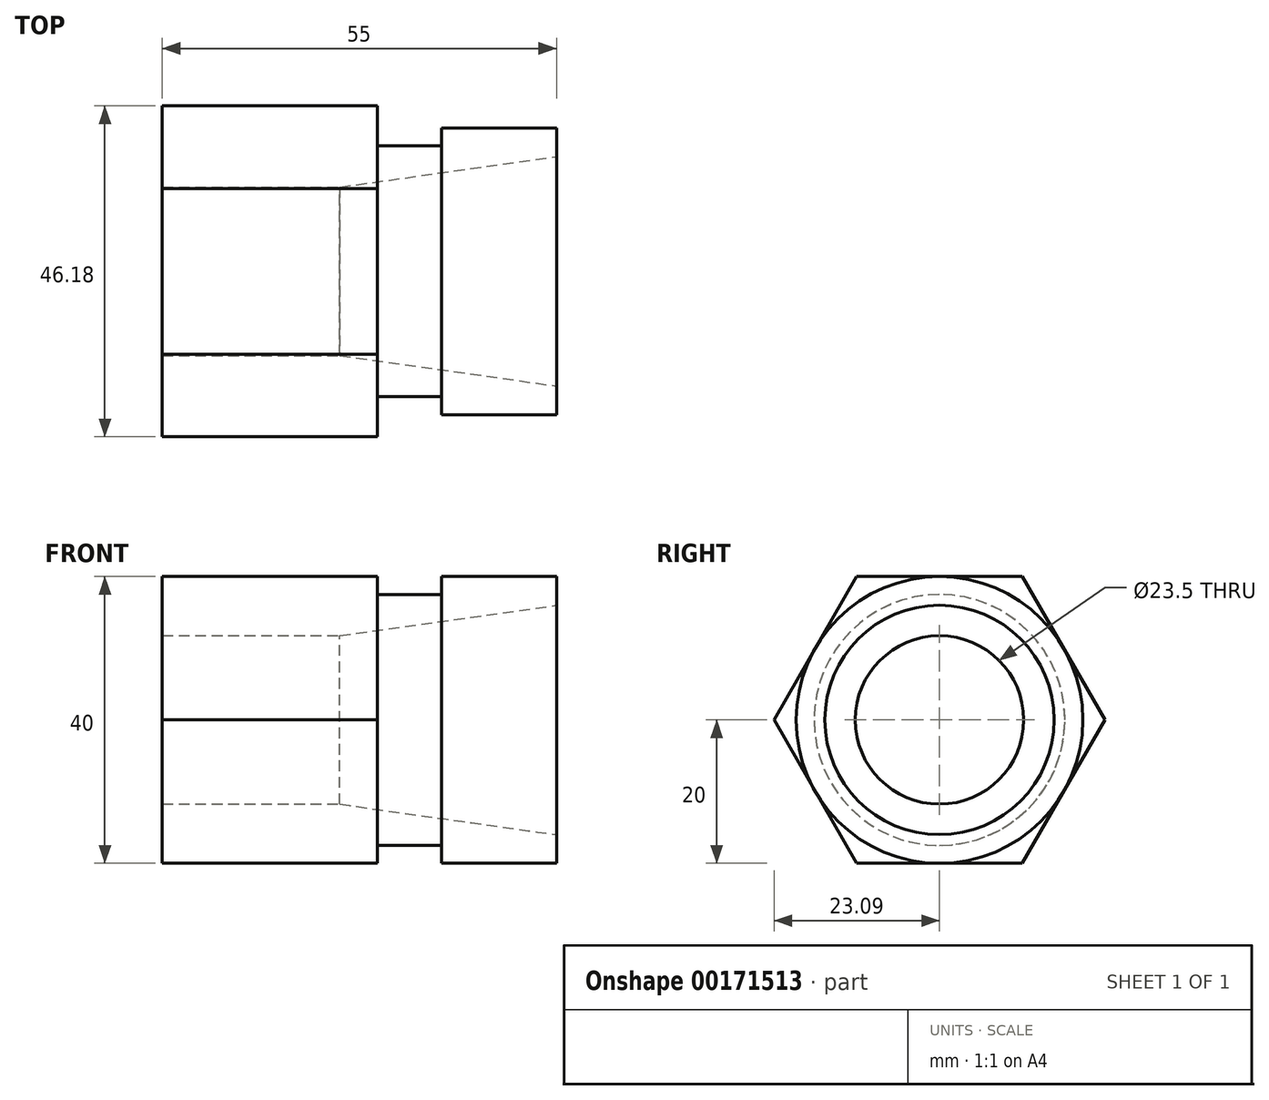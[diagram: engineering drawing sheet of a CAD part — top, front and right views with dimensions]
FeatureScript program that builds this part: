
annotation { "Feature Type Name" : "Feature", "Feature Type Description" : "" }
export const myFeature = defineFeature(function(context is Context, id is Id, definition is map)
    precondition{}
    {
        {
            var Q0;
            Q0=qCreatedBy(makeId("Front.planeOp"),FACE);
            var sketch = newSketch(context, id + "F0", { "sketchPlane" : qUnion([Q0])});
            skLineSegment(sketch, "E0", {"start": v(0, 0) * mm, "end": v(-55, 0) * mm, "construction": true});
            skLineSegment(sketch, "E1", {"start": v(-55, 0) * mm, "end": v(-55, 17.5) * mm});
            skLineSegment(sketch, "E2", {"start": v(-16, 20) * mm, "end": v(0, 20) * mm});
            skLineSegment(sketch, "E3", {"start": v(0, 20) * mm, "end": v(0, 16) * mm});
            skLineSegment(sketch, "E4", {"start": v(0, 16) * mm, "end": v(-30.24, 11.75) * mm});
            skLineSegment(sketch, "E5", {"start": v(-30.24, 11.75) * mm, "end": v(-34, 11.75) * mm});
            skLineSegment(sketch, "E6", {"start": v(-34, 11.75) * mm, "end": v(-36.93, 0) * mm});
            skLineSegment(sketch, "E7", {"start": v(-36.93, 0) * mm, "end": v(-55, 0) * mm});
            skLineSegment(sketch, "E8", {"start": v(-30.24, 11.75) * mm, "end": v(-3.23, 11.75) * mm, "construction": true});
            skLineSegment(sketch, "E9.top", {"start": v(-55, 17.5) * mm, "end": v(-16, 17.5) * mm});
            skLineSegment(sketch, "E9.right", {"start": v(-16, 20) * mm, "end": v(-16, 17.5) * mm});
            skSolve(sketch);
        }
        {
            var Q0;
            Q0=makeQuery(id+"F0.imprint","IMPRINT",FACE,{"disambiguationData":[TD([[makeQuery(id+"F0.imprint","IMPRINT",EDGE,{"derivedFrom":sQuery(id+"F0.wireOp",EDGE,"E1")}),-1.0]])]});
            var Q1;
            Q1=sQuery(id+"F0.wireOp",EDGE,"E0");
            revolve(context, id + "F1", {"entities" : qUnion([Q0]), "axis" : qUnion([Q1]), "revolveType" : RevolveType.FULL});
        }
        {
            var Q0;
            Q0=makeQuery(id+"F1.opRevolve","SWEPT_FACE",FACE,{"disambiguationData":[OSD([sQuery(id+"F0.wireOp",EDGE,"E1")])]});
            var sketch = newSketch(context, id + "F2", { "sketchPlane" : qUnion([Q0])});
            skCircle(sketch, "E10.cCircle", {"center": v(0, 0) * mm, "radius": 23.1 * mm, "construction": true});
            skLineSegment(sketch, "E10.0", {"start": v(23.1, 0) * mm, "end": v(11.55, -20) * mm});
            skLineSegment(sketch, "E10.1", {"start": v(11.55, -20) * mm, "end": v(-11.55, -20) * mm});
            skLineSegment(sketch, "E10.2", {"start": v(-11.55, -20) * mm, "end": v(-23.1, 0) * mm});
            skLineSegment(sketch, "E10.3", {"start": v(-23.1, 0) * mm, "end": v(-11.55, 20) * mm});
            skLineSegment(sketch, "E10.4", {"start": v(-11.55, 20) * mm, "end": v(11.55, 20) * mm});
            skLineSegment(sketch, "E10.5", {"start": v(11.55, 20) * mm, "end": v(23.1, 0) * mm});
            skSolve(sketch);
        }
        {
            var Q0;
            Q0=makeQuery(id+"F2.imprint","IMPRINT",FACE,{"disambiguationData":[TD([[makeQuery(id+"F2.imprint","IMPRINT",EDGE,{"derivedFrom":sQuery(id+"F2.wireOp",EDGE,"E10.0")}),-1.0]])]});
            extrude(context, id + "F3", {"entities" : qUnion([Q0]), "operationType" : NewBodyOperationType.ADD, "oppositeDirection" : true, "depth" : 30 * mm});
        }
        {
            var Q0;
            Q0=makeQuery(id+"F3.boolean.opBoolean","MERGE",FACE,{"derivedFrom":[makeQuery(id+"F1.opRevolve","SWEPT_FACE",FACE,{"disambiguationData":[OSD([sQuery(id+"F0.wireOp",EDGE,"E1")])]}),makeQuery(id+"F3.opExtrude","CAP_FACE",FACE,{"disambiguationData":[OSD([sQuery(id+"F2.wireOp",EDGE,"E10.0"),sQuery(id+"F2.wireOp",EDGE,"E10.1"),sQuery(id+"F2.wireOp",EDGE,"E10.2"),sQuery(id+"F2.wireOp",EDGE,"E10.3"),sQuery(id+"F2.wireOp",EDGE,"E10.4"),sQuery(id+"F2.wireOp",EDGE,"E10.5")])],"isStart":true})]});
            var sketch = newSketch(context, id + "F4", { "sketchPlane" : qUnion([Q0])});
            skCircle(sketch, "E11", {"center": v(0, 0) * mm, "radius": 11.75 * mm});
            skSolve(sketch);
        }
        {
            var Q0;
            Q0=makeQuery(id+"F4.imprint","IMPRINT",FACE,{"disambiguationData":[TD([[makeQuery(id+"F4.imprint","IMPRINT",EDGE,{"derivedFrom":sQuery(id+"F4.wireOp",EDGE,"E11")}),1.0]])]});
            extrude(context, id + "F5", {"entities" : qUnion([Q0]), "operationType" : NewBodyOperationType.REMOVE, "endBound" : BoundingType.THROUGH_ALL, "oppositeDirection" : true, "depth" : 25 * mm});
        }
    });
